# Revit family: 138086841_Mueble Elipse Plus 80 cm con Lavamanos.pdf
name_source: partatom
category: Furniture
units: mm (PartAtom-declared; Revit-internal decimal feet)

## family parameters
Always vertical = Yes
Cut with Voids When Loaded = No
OmniClass Number = 23.31.13.11
OmniClass Title = Single Sinks
Room Calculation Point = No
Shared = No
Work Plane-Based = No

## types (1)
- 138086841_Mueble Elipse Plus 80 cm con Lavamanos.pdf
    Acabado = Corona_Ambar
    Alto = 500 mm  [stored 1.64042 ft]
    Ancho = 800 mm  [stored 2.62467 ft]
    Creado por = IDD
    Description = Línea de Muebles Elipse Plus con mezcla de materiales y manija en aluminio
que brindan un diseño moderno, en formato de 60 y 80 cm con una puerta y
una canastilla organizadora. Máxima capacidad de almacenamiento.
· Resistentes a la humedad.
· Lavamanos 100% en porcelana.
· Canastilla Organizadora
    Fecha de creación = 28/07/2020
    Garantía = 5 Años (Madera)
    Garantía Herraje = 1 año
    Longitud = 453 mm  [stored 1.48622 ft]
    Manija = Corona_Aluminio
    Manufacturer = Corona
    Material = Corona_Madera_Niebla
    Model = Elipse Plus 60
    Peso Bruto aprox = 43,9 lb (19,9 kg).
    Peso Neto aprox = 35,7 lb (16,2 kg).
    Resistencia a la humedad = 8%
    Resistencia al rayado = 700 ciclos
    URL = https://corona.co

note: [stored X ft] marks values corroborated as IEEE doubles in the binary element streams (Revit-internal decimal feet)

## geometry (parser evidence)
native form markers: Sweep x14
no freeform markers — native parametric forms only
